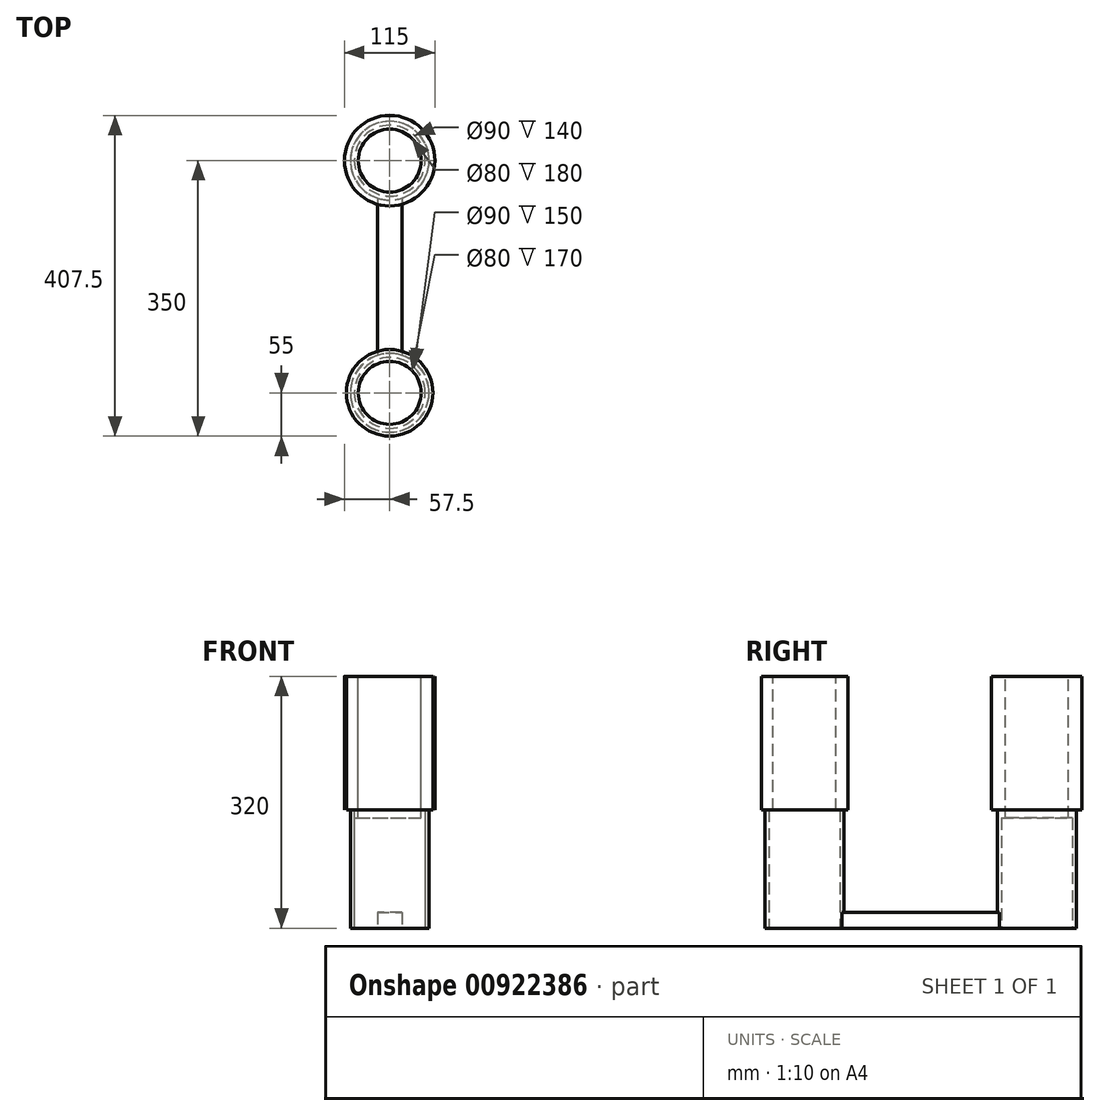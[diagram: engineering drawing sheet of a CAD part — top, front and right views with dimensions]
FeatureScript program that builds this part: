
annotation { "Feature Type Name" : "Feature", "Feature Type Description" : "" }
export const myFeature = defineFeature(function(context is Context, id is Id, definition is map)
    precondition{}
    {
        {
            var Q0;
            Q0=qCreatedBy(makeId("Top.planeOp"),FACE);
            var sketch = newSketch(context, id + "F0", { "sketchPlane" : qUnion([Q0])});
            skCircle(sketch, "E0", {"center": v(0, 0) * mm, "radius": 50 * mm});
            skSolve(sketch);
        }
        {
            var Q0;
            Q0 = qSketchRegion(id + "F0", true);
            extrude(context, id + "F1", {"entities" : qUnion([Q0]), "depth" : 150 * mm, "offsetDistance" : 25 * mm});
        }
        {
            var Q0;
            Q0=makeQuery(id+"F1.opExtrude","CAP_FACE",FACE,{"disambiguationData":[OSD([sQuery(id+"F0.wireOp",EDGE,"E0")])],"isStart":true});
            var sketch = newSketch(context, id + "F2", { "sketchPlane" : qUnion([Q0])});
            skCircle(sketch, "E1", {"center": v(0, 0) * mm, "radius": 45 * mm});
            skSolve(sketch);
        }
        {
            var Q0;
            Q0 = qSketchRegion(id + "F2", true);
            extrude(context, id + "F3", {"entities" : qUnion([Q0]), "operationType" : NewBodyOperationType.REMOVE, "oppositeDirection" : true, "depth" : 140 * mm, "offsetDistance" : 25 * mm});
        }
        {
            var Q0;
            Q0=makeQuery(id+"F1.opExtrude","CAP_FACE",FACE,{"disambiguationData":[OSD([sQuery(id+"F0.wireOp",EDGE,"E0")])],"isStart":false});
            var sketch = newSketch(context, id + "F4", { "sketchPlane" : qUnion([Q0])});
            skCircle(sketch, "E2", {"center": v(0, 0) * mm, "radius": 57.5 * mm});
            skSolve(sketch);
        }
        {
            var Q0;
            Q0 = qSketchRegion(id + "F4", true);
            extrude(context, id + "F5", {"entities" : qUnion([Q0]), "operationType" : NewBodyOperationType.ADD, "depth" : 170 * mm, "offsetDistance" : 25 * mm});
        }
        {
            var Q0;
            Q0=makeQuery(id+"F5.opExtrude","CAP_FACE",FACE,{"disambiguationData":[OSD([sQuery(id+"F4.wireOp",EDGE,"E2")])],"isStart":false});
            var sketch = newSketch(context, id + "F6", { "sketchPlane" : qUnion([Q0])});
            skCircle(sketch, "E3", {"center": v(0, 0) * mm, "radius": 40 * mm});
            skSolve(sketch);
        }
        {
            var Q0;
            Q0 = qSketchRegion(id + "F6", true);
            extrude(context, id + "F7", {"entities" : qUnion([Q0]), "operationType" : NewBodyOperationType.REMOVE, "oppositeDirection" : true, "depth" : 383 * mm, "offsetDistance" : 25 * mm});
        }
        {
            var Q0;
            Q0=makeQuery(id+"F1.opExtrude","CAP_FACE",FACE,{"disambiguationData":[OSD([sQuery(id+"F0.wireOp",EDGE,"E0")])],"isStart":true});
            var sketch = newSketch(context, id + "F8", { "sketchPlane" : qUnion([Q0])});
            skLineSegment(sketch, "E4.bottom", {"start": v(-15.61, 47.5) * mm, "end": v(15.61, 47.5) * mm});
            skLineSegment(sketch, "E4.top", {"start": v(-15.61, 247.5) * mm, "end": v(15.61, 247.5) * mm});
            skLineSegment(sketch, "E4.left", {"start": v(-15.61, 47.5) * mm, "end": v(-15.61, 247.5) * mm});
            skLineSegment(sketch, "E4.right", {"start": v(15.61, 47.5) * mm, "end": v(15.61, 247.5) * mm});
            skSolve(sketch);
        }
        {
            var Q0;
            Q0 = qSketchRegion(id + "F8", true);
            extrude(context, id + "F9", {"entities" : qUnion([Q0]), "operationType" : NewBodyOperationType.ADD, "oppositeDirection" : true, "depth" : 20 * mm, "offsetDistance" : 25 * mm});
        }
        {
            var Q0;
            Q0=makeQuery(id+"F9.boolean.opBoolean","MERGE",FACE,{"derivedFrom":[makeQuery(id+"F1.opExtrude","CAP_FACE",FACE,{"disambiguationData":[OSD([sQuery(id+"F0.wireOp",EDGE,"E0")])],"isStart":true}),makeQuery(id+"F9.opExtrude","CAP_FACE",FACE,{"disambiguationData":[OSD([sQuery(id+"F8.wireOp",EDGE,"E4.bottom"),sQuery(id+"F8.wireOp",EDGE,"E4.top"),sQuery(id+"F8.wireOp",EDGE,"E4.left"),sQuery(id+"F8.wireOp",EDGE,"E4.right")])],"isStart":true})]});
            var sketch = newSketch(context, id + "F10", { "sketchPlane" : qUnion([Q0])});
            skLineSegment(sketch, "E5", {"start": v(0, 247.5) * mm, "end": v(0, 295) * mm, "construction": true});
            skCircle(sketch, "E6", {"center": v(0, 295) * mm, "radius": 50 * mm});
            skSolve(sketch);
        }
        {
            var Q0;
            Q0 = qSketchRegion(id + "F10", true);
            extrude(context, id + "F11", {"entities" : qUnion([Q0]), "operationType" : NewBodyOperationType.ADD, "oppositeDirection" : true, "depth" : 150 * mm, "offsetDistance" : 25 * mm});
        }
        {
            var Q0;
            Q0=makeQuery(id+"F11.boolean.opBoolean","MERGE",FACE,{"derivedFrom":[makeQuery(id+"F9.boolean.opBoolean","MERGE",FACE,{"derivedFrom":[makeQuery(id+"F1.opExtrude","CAP_FACE",FACE,{"disambiguationData":[OSD([sQuery(id+"F0.wireOp",EDGE,"E0")])],"isStart":true}),makeQuery(id+"F9.opExtrude","CAP_FACE",FACE,{"disambiguationData":[OSD([sQuery(id+"F8.wireOp",EDGE,"E4.bottom"),sQuery(id+"F8.wireOp",EDGE,"E4.top"),sQuery(id+"F8.wireOp",EDGE,"E4.left"),sQuery(id+"F8.wireOp",EDGE,"E4.right")])],"isStart":true})]}),makeQuery(id+"F11.opExtrude","CAP_FACE",FACE,{"disambiguationData":[OSD([sQuery(id+"F10.wireOp",EDGE,"E6")])],"isStart":true})]});
            var sketch = newSketch(context, id + "F12", { "sketchPlane" : qUnion([Q0])});
            skCircle(sketch, "E7", {"center": v(0, 295) * mm, "radius": 45 * mm});
            skSolve(sketch);
        }
        {
            var Q0;
            Q0 = qSketchRegion(id + "F12", true);
            extrude(context, id + "F13", {"entities" : qUnion([Q0]), "operationType" : NewBodyOperationType.REMOVE, "oppositeDirection" : true, "depth" : 150 * mm, "offsetDistance" : 25 * mm});
        }
        {
            var Q0;
            Q0=makeQuery(id+"F11.opExtrude","CAP_FACE",FACE,{"disambiguationData":[OSD([sQuery(id+"F10.wireOp",EDGE,"E6")])],"isStart":false});
            var sketch = newSketch(context, id + "F14", { "sketchPlane" : qUnion([Q0])});
            skCircle(sketch, "E8", {"center": v(0, -295) * mm, "radius": 55 * mm});
            skSolve(sketch);
        }
        {
            var Q0;
            Q0 = qSketchRegion(id + "F14", true);
            extrude(context, id + "F15", {"entities" : qUnion([Q0]), "operationType" : NewBodyOperationType.ADD, "depth" : 170 * mm, "offsetDistance" : 25 * mm});
        }
        {
            var Q0;
            Q0=makeQuery(id+"F15.opExtrude","CAP_FACE",FACE,{"disambiguationData":[OSD([sQuery(id+"F14.wireOp",EDGE,"E8")])],"isStart":false});
            var sketch = newSketch(context, id + "F16", { "sketchPlane" : qUnion([Q0])});
            skCircle(sketch, "E9", {"center": v(0, -295) * mm, "radius": 40 * mm});
            skSolve(sketch);
        }
        {
            var Q0;
            Q0 = qSketchRegion(id + "F16", true);
            extrude(context, id + "F17", {"entities" : qUnion([Q0]), "operationType" : NewBodyOperationType.REMOVE, "oppositeDirection" : true, "depth" : 5000 * mm, "offsetDistance" : 25 * mm});
        }
    });
